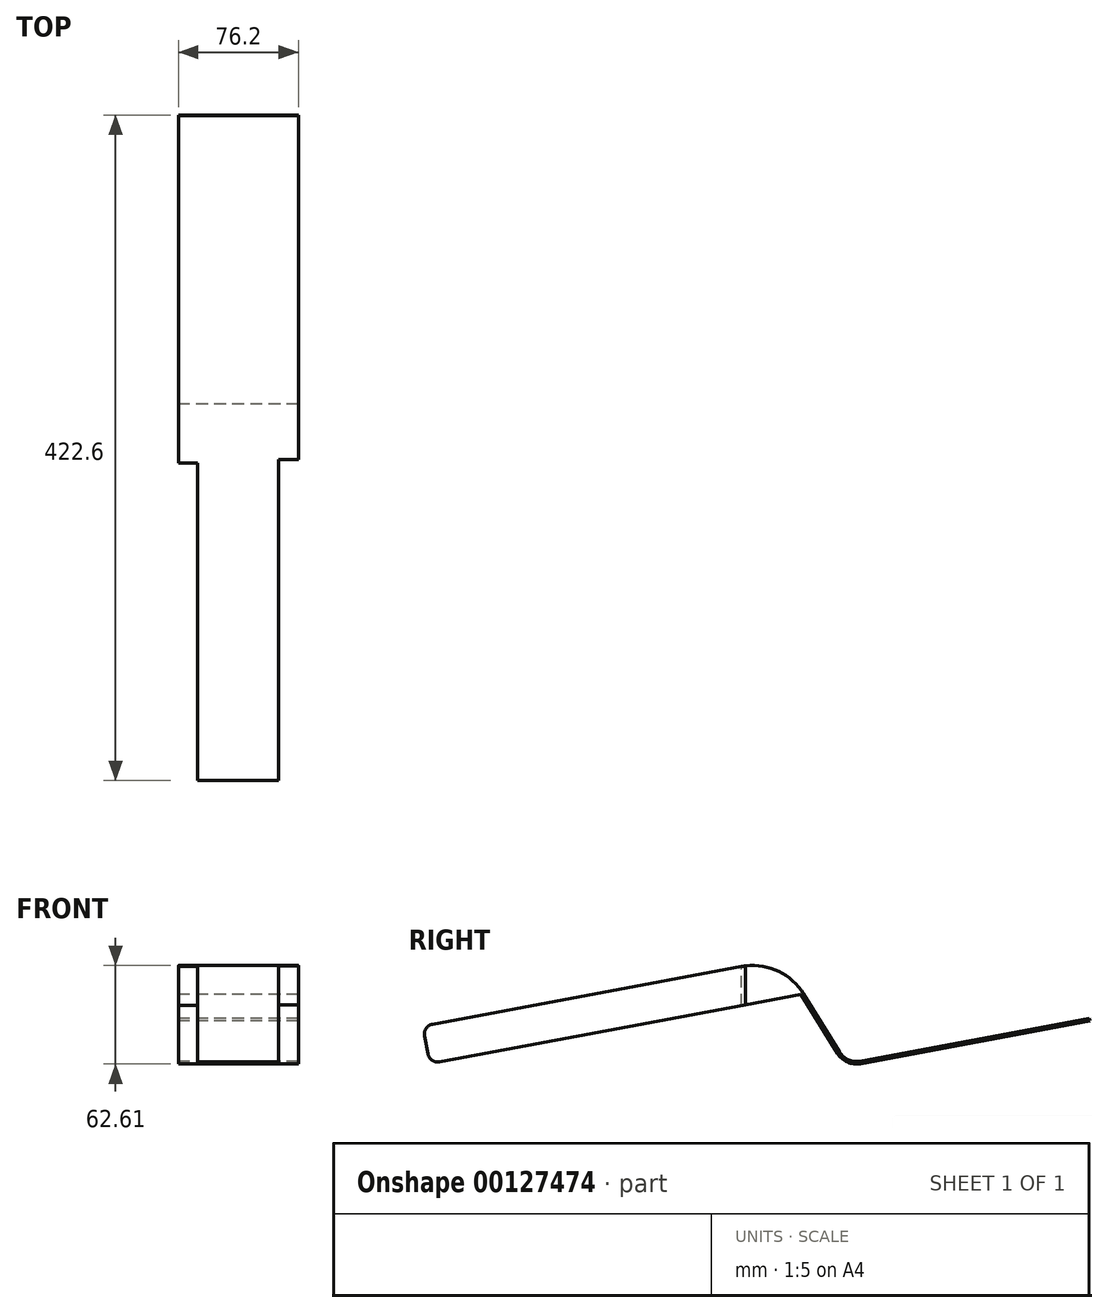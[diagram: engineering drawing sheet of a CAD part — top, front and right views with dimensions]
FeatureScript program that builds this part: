
annotation { "Feature Type Name" : "Feature", "Feature Type Description" : "" }
export const myFeature = defineFeature(function(context is Context, id is Id, definition is map)
    precondition{}
    {
        {
            var Q0;
            Q0=qCreatedBy(makeId("Right.planeOp"),FACE);
            var sketch = newSketch(context, id + "F0", { "sketchPlane" : qUnion([Q0])});
            skLineSegment(sketch, "E0", {"start": v(8.57, 1.6) * mm, "end": v(154.09, 28.74) * mm});
            skLineSegment(sketch, "E1", {"start": v(-4.57, 7.42) * mm, "end": v(-27.31, 44.3) * mm});
            skLineSegment(sketch, "E2", {"start": v(-66.73, 61.75) * mm, "end": v(-263.04, 25.14) * mm});
            skPoint(sketch, "E3.visualSharp", {"position": v(-41.03, 66.54) * mm});
            skArc(sketch, "E3.filletArc", {"start": v(-27.31, 44.3) * mm, "mid": v(-44.31, 59.13) * mm, "end": v(-66.73, 61.75) * mm});
            skLineSegment(sketch, "E4", {"start": v(-28.99, 43.98) * mm, "end": v(-258.57, 1.16) * mm});
            skLineSegment(sketch, "E5", {"start": v(0, 0) * mm, "end": v(-264.8, 0) * mm, "construction": true});
            skLineSegment(sketch, "E6", {"start": v(-265.97, 6.24) * mm, "end": v(-268.12, 17.73) * mm});
            skPoint(sketch, "E7.visualSharp", {"position": v(0, 0) * mm});
            skArc(sketch, "E7.filletArc", {"start": v(-4.57, 7.42) * mm, "mid": v(1.1, 2.47) * mm, "end": v(8.57, 1.6) * mm});
            skLineSegment(sketch, "E8.0", {"start": v(8.86, 0.04) * mm, "end": v(154.38, 27.18) * mm});
            skArc(sketch, "E8.1", {"start": v(-5.92, 6.58) * mm, "mid": v(0.45, 1.02) * mm, "end": v(8.86, 0.04) * mm});
            skLineSegment(sketch, "E8.2", {"start": v(-5.92, 6.58) * mm, "end": v(-28.66, 43.46) * mm});
            skLineSegment(sketch, "E9", {"start": v(-28.66, 43.46) * mm, "end": v(-28.99, 43.98) * mm});
            skLineSegment(sketch, "E10", {"start": v(154.38, 27.18) * mm, "end": v(154.09, 28.74) * mm});
            skPoint(sketch, "E11.visualSharp", {"position": v(-264.8, 0) * mm});
            skArc(sketch, "E11.filletArc", {"start": v(-265.97, 6.24) * mm, "mid": v(-263.32, 2.17) * mm, "end": v(-258.57, 1.16) * mm});
            skPoint(sketch, "E12.visualSharp", {"position": v(-269.28, 23.97) * mm});
            skArc(sketch, "E12.filletArc", {"start": v(-263.04, 25.14) * mm, "mid": v(-267.11, 22.49) * mm, "end": v(-268.12, 17.73) * mm});
            skSolve(sketch);
        }
        {
            var Q0;
            Q0 = qSketchRegion(id + "F0", true);
            extrude(context, id + "F1", {"entities" : qUnion([Q0]), "endBound" : BoundingType.SYMMETRIC, "depth" : 76.2 * mm});
        }
        {
            var Q0;
            Q0=qCreatedBy(makeId("Top.planeOp"),FACE);
            var sketch = newSketch(context, id + "F2", { "sketchPlane" : qUnion([Q0])});
            skLineSegment(sketch, "E13.bottom", {"start": v(25.55, -283.94) * mm, "end": v(-26.08, -283.94) * mm});
            skLineSegment(sketch, "E13.left", {"start": v(25.55, -283.94) * mm, "end": v(25.55, -64.22) * mm});
            skLineSegment(sketch, "E13.right", {"start": v(-26.08, -283.94) * mm, "end": v(-26.08, -66.73) * mm});
            skLineSegment(sketch, "E14", {"start": v(-0.26, -283.94) * mm, "end": v(0, 0) * mm, "construction": true});
            skLineSegment(sketch, "E15", {"start": v(25.55, -64.22) * mm, "end": v(75.22, -64.22) * mm});
            skLineSegment(sketch, "E16", {"start": v(75.22, -64.22) * mm, "end": v(82.36, -321.52) * mm});
            skLineSegment(sketch, "E17", {"start": v(82.36, -321.52) * mm, "end": v(-85.92, -313.58) * mm});
            skLineSegment(sketch, "E18", {"start": v(-85.92, -313.58) * mm, "end": v(-80.36, -214.37) * mm});
            skLineSegment(sketch, "E19", {"start": v(-80.36, -214.37) * mm, "end": v(-80.36, -66.73) * mm});
            skLineSegment(sketch, "E20", {"start": v(-80.36, -66.73) * mm, "end": v(-26.08, -66.73) * mm});
            skSolve(sketch);
        }
        {
            var Q0;
            Q0 = qSketchRegion(id + "F2", true);
            extrude(context, id + "F3", {"entities" : qUnion([Q0]), "operationType" : NewBodyOperationType.REMOVE, "depth" : 128.12 * mm});
        }
    });
